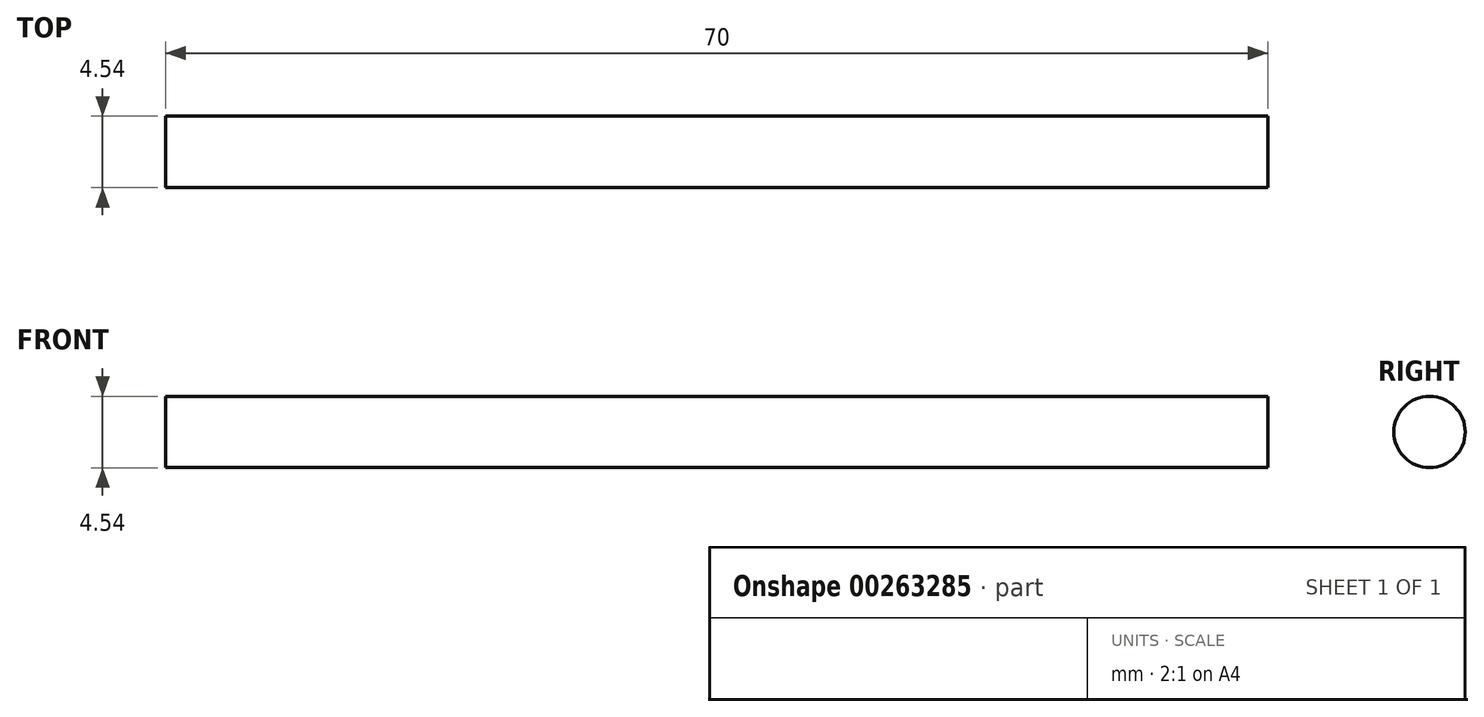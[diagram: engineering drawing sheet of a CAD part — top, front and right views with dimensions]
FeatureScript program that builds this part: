
annotation { "Feature Type Name" : "Feature", "Feature Type Description" : "" }
export const myFeature = defineFeature(function(context is Context, id is Id, definition is map)
    precondition{}
    {
        {
            var Q0;
            Q0=qCreatedBy(makeId("Right.planeOp"),FACE);
            var sketch = newSketch(context, id + "F0", { "sketchPlane" : qUnion([Q0])});
            skCircle(sketch, "E0", {"center": v(0, 0) * mm, "radius": 2.27 * mm});
            skSolve(sketch);
        }
        {
            var Q0;
            Q0 = qSketchRegion(id + "F0", true);
            extrude(context, id + "F1", {"entities" : qUnion([Q0]), "depth" : 70 * mm});
        }
    });
